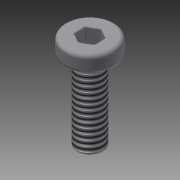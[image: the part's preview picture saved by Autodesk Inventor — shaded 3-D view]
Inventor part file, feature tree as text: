
AUTODESK INVENTOR PART (.ipt)
format: ipt  version: 2013 (Build 170138000, 138)  size: 157,696 bytes
history: native  units: mm
features: extrude x3, sketch x3, fillet x2, other x1, thread x1
ambient origin geometry x1: Origin
feature tree (10):
  other  "ソリッド1"
  extrude  "押し出し1"  Depth=3.8mm
  extrude  "押し出し2"  Depth=1.3mm TaperAngle=0.0deg
  extrude  "押し出し3"  Depth=2.0mm
  fillet  "フィレット1"  Radius=6.0mm
  fillet  "フィレット2"  Radius=0.75mm
  thread  "ねじ3"
  sketch  "スケッチ1"
  sketch  "スケッチ2"
  sketch  "スケッチ3"
